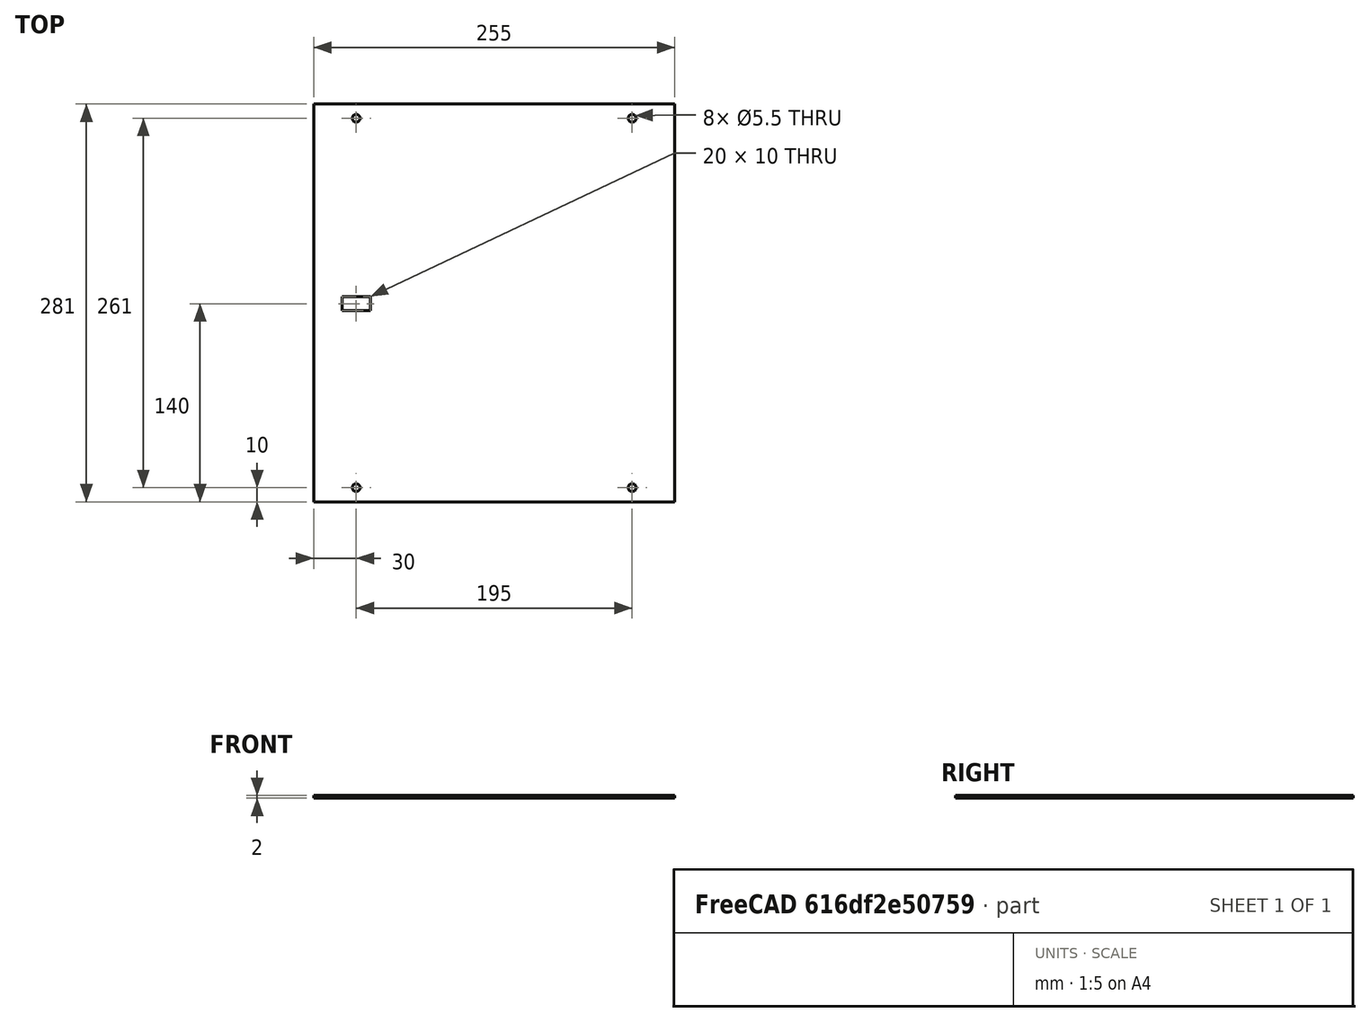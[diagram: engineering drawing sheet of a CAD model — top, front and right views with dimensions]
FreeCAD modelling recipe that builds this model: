
FCSTD DOCUMENT  (FreeCAD 0.15R4671 (Git))
Label: top
License: All rights reserved
LicenseURL: http://en.wikipedia.org/wiki/All_rights_reserved
objects: Drawing::FeatureViewPython×15, Part::Cut×6, Part::Cylinder×4, Part::Box×2, Drawing::FeatureViewPart×1, Drawing::FeaturePage×1
note: 12 computed .brp shape members not serialized (recipe doc carries the construction recipe); baked Part::Feature solids carry a one-line shape summary decoded from their .brp

FEATURE [Part::Box] Box  label="Cube"
  Height = 2
  Length = 255
  Placement = pos=(0,0,1.5332e-08) rot=(0,0,1;0rad)
  Width = 281
FEATURE [Part::Cylinder] Cylinder
  Angle = 360
  Height = 10
  Placement = pos=(30,10,-5) rot=(0,0,1;0rad)
  Radius = 2.75
FEATURE [Part::Cylinder] Cylinder001
  Angle = 360
  Height = 10
  Placement = pos=(30,271,-5) rot=(0,0,1;0rad)
  Radius = 2.75
FEATURE [Part::Cylinder] Cylinder002
  Angle = 360
  Height = 10
  Placement = pos=(225,10,-5) rot=(0,0,1;0rad)
  Radius = 2.75
FEATURE [Part::Cylinder] Cylinder003
  Angle = 360
  Height = 10
  Placement = pos=(225,271,-5) rot=(0,0,1;0rad)
  Radius = 2.75
FEATURE [Part::Cut] Cut
  Base = -> Box
  Tool = -> Cylinder
FEATURE [Part::Cut] Cut001
  Base = -> Cut
  Tool = -> Cylinder001
FEATURE [Part::Cut] Cut002
  Base = -> Cut001
  Tool = -> Cylinder002
FEATURE [Part::Cut] Cut003  label="top"
  Base = -> Cut002
  Tool = -> Cylinder003
FEATURE [Part::Box] Box001  label="Cube001"
  Height = 10
  Length = 20
  Placement = pos=(20,135,-5) rot=(0,0,1;0rad)
  Width = 10
FEATURE [Part::Cut] Cut004
  Base = -> Cut002
  Tool = -> Cylinder003
FEATURE [Part::Cut] Cut005
  Base = -> Cut003
  Tool = -> Box001
FEATURE [Drawing::FeatureViewPart] Ortho  label="Ortho_0_0"
  Direction = (0,0,1)
  HiddenWidth = 0.15
  LineWidth = 0.35
  Rotation = 0
  Scale = 0.5
  ShowHiddenLines = false
  ShowSmoothLines = false
  Source = -> Cut005
  Tolerance = 0.05
  ViewResult = <g id="Ortho_0_0"\n   transform="rotate(0,46.25,188.75) translate(46.25,188.75) scale(0.5,0.5)"\n  >\n<g   stroke="rgb(0, 0, 0)"\n   stroke-width="0.7"\n   stroke-linecap="butt"\n   stroke-linejoin="miter"\n   fill="none"\n   transform="scale(1,-1)"\n  >\n<path id= "1" d=" M 0 0 L 0 281 " />\n<path id= "2" d=" M 0 0 L 255 0 " />\n<path id= "3" d=" M 0 281 L 255 281 " />\n<path id= "4" d=" M 255 0 L 255 281 " />\n<circle cx ="30" cy ="10" r ="2.75" /><circle cx ="225" cy ="10" r ="2.75" /><path id= "7" d=" M 40 145 L 20 145 " />\n<path id= "8" d=" M 20 135 L 20 145 " />\n<path id= "9" d=" M 40 135 L 20 135 " />\n<path id= "10" d=" M 40 135 L 40 145 " />\n<circle cx ="225" cy ="271" r ="2.75" /><circle cx ="30" cy ="271" r ="2.75" /></g>\n</g>
  Visible = true
  X = 46.25
  Y = 188.75
FEATURE [Drawing::FeatureViewPython] dim001  # drawing view (typed FeaturePython)
  Rotation = 0
  ViewResult = <g> \n  <line x1="44.250000" y1="188.750000" x2="32.514934" y2="188.750000" style="stroke:rgb(0,0,255);stroke-width:0.50" />\n<line x1="44.250000" y1="48.250000" x2="32.514934" y2="48.250000" style="stroke:rgb(0,0,255);stroke-width:0.50" />\n<line x1="33.514934" y1="188.750000" x2="33.514934" y2="48.250000" style="stroke:rgb(0,0,255);stroke-width:0.50" /> \n  <polygon points="33.514934,48.250000 32.514934,51.250000 33.514934,52.250000 34.514934,51.250000" style="fill:rgb(0,0,255);stroke:rgb(0,0,255);stroke-width:0" /><polygon points="33.514934,188.750000 34.514934,185.750000 33.514934,184.750000 32.514934,185.750000" style="fill:rgb(0,0,255);stroke:rgb(0,0,255);stroke-width:0" /> \n  <text x="31.514934" y="118.500000" font-family="inherit" font-size="3.6" fill="rgb(0,0,255)" text-anchor="middle" transform="rotate(-90.000000 31.514934,118.500000)" >281</text> </g>
  Visible = true
  X = 0
  Y = 0
  arrowL1 = 3
  arrowL2 = 1
  arrowW = 2
  arrow_scheme = 0
  autoPlaceOffset = 2
  autoPlaceText = true
  click1_x = 33.5149
  click1_y = 120.857
  click2_x = 33.5149
  click2_y = 120.857
  comma_decimal_place = false
  dimension_line_overshoot = 1
  gap_datum_points = 2
  halfDimension_linear = false
  lineColor = rgb(0,0,255)
  strokeWidth = 0.5
  textFormat_linear = %(value)f
  textRenderer_color = rgb(0,0,255)
  textRenderer_family = inherit
  textRenderer_size = 3.6
  unit_custom_scale = 1
  unit_scheme = 0
FEATURE [Drawing::FeatureViewPython] dim002  # drawing view (typed FeaturePython)
  Rotation = 0
  ViewResult = <g> \n  <line x1="46.250000" y1="46.250000" x2="46.250000" y2="32.176400" style="stroke:rgb(0,0,255);stroke-width:0.50" />\n<line x1="173.750000" y1="46.250000" x2="173.750000" y2="32.176400" style="stroke:rgb(0,0,255);stroke-width:0.50" />\n<line x1="46.250000" y1="33.176400" x2="173.750000" y2="33.176400" style="stroke:rgb(0,0,255);stroke-width:0.50" /> \n  <polygon points="173.750000,33.176400 170.750000,32.176400 169.750000,33.176400 170.750000,34.176400" style="fill:rgb(0,0,255);stroke:rgb(0,0,255);stroke-width:0" /><polygon points="46.250000,33.176400 49.250000,34.176400 50.250000,33.176400 49.250000,32.176400" style="fill:rgb(0,0,255);stroke:rgb(0,0,255);stroke-width:0" /> \n  <text x="110.000000" y="31.176400" font-family="inherit" font-size="3.6" fill="rgb(0,0,255)" text-anchor="middle" transform="rotate(0.000000 110.000000,31.176400)" >255</text> </g>
  Visible = true
  X = 0
  Y = 0
  arrowL1 = 3
  arrowL2 = 1
  arrowW = 2
  arrow_scheme = 0
  autoPlaceOffset = 2
  autoPlaceText = true
  click1_x = 106.3
  click1_y = 33.1764
  click2_x = 106.3
  click2_y = 33.1764
  comma_decimal_place = false
  dimension_line_overshoot = 1
  gap_datum_points = 2
  halfDimension_linear = false
  lineColor = rgb(0,0,255)
  strokeWidth = 0.5
  textFormat_linear = %(value)f
  textRenderer_color = rgb(0,0,255)
  textRenderer_family = inherit
  textRenderer_size = 3.6
  unit_custom_scale = 1
  unit_scheme = 0
FEATURE [Drawing::FeatureViewPython] dim003  # drawing view (typed FeaturePython)
  Rotation = 0
  ViewResult = <g> \n  <line x1="66.250000" y1="114.250000" x2="66.250000" y2="105.638428" style="stroke:rgb(0,0,255);stroke-width:0.50" />\n<line x1="56.250000" y1="114.250000" x2="56.250000" y2="105.638428" style="stroke:rgb(0,0,255);stroke-width:0.50" />\n<line x1="66.250000" y1="106.638428" x2="56.250000" y2="106.638428" style="stroke:rgb(0,0,255);stroke-width:0.50" /> \n  <polygon points="56.250000,106.638428 53.250000,105.638428 52.250000,106.638428 53.250000,107.638428" style="fill:rgb(0,0,255);stroke:rgb(0,0,255);stroke-width:0" /><polygon points="66.250000,106.638428 69.250000,107.638428 70.250000,106.638428 69.250000,105.638428" style="fill:rgb(0,0,255);stroke:rgb(0,0,255);stroke-width:0" /> \n  <text x="61.250000" y="104.638428" font-family="inherit" font-size="3.6" fill="rgb(0,0,255)" text-anchor="middle" transform="rotate(0.000000 61.250000,104.638428)" >20</text> </g>
  Visible = true
  X = 0
  Y = 0
  arrowL1 = 3
  arrowL2 = 1
  arrowW = 2
  arrow_scheme = 0
  autoPlaceOffset = 2
  autoPlaceText = true
  click1_x = 62.6289
  click1_y = 106.638
  click2_x = 62.6289
  click2_y = 106.638
  comma_decimal_place = false
  dimension_line_overshoot = 1
  gap_datum_points = 2
  halfDimension_linear = false
  lineColor = rgb(0,0,255)
  strokeWidth = 0.5
  textFormat_linear = %(value)f
  textRenderer_color = rgb(0,0,255)
  textRenderer_family = inherit
  textRenderer_size = 3.6
  unit_custom_scale = 1
  unit_scheme = 0
FEATURE [Drawing::FeatureViewPython] dim004  # drawing view (typed FeaturePython)
  Rotation = 0
  ViewResult = <g> \n  <line x1="68.250000" y1="121.250000" x2="81.478770" y2="121.250000" style="stroke:rgb(0,0,255);stroke-width:0.50" />\n<line x1="68.250000" y1="116.250000" x2="81.478770" y2="116.250000" style="stroke:rgb(0,0,255);stroke-width:0.50" />\n<line x1="80.478770" y1="121.250000" x2="80.478770" y2="116.250000" style="stroke:rgb(0,0,255);stroke-width:0.50" /> \n  <polygon points="80.478770,116.250000 81.478770,113.250000 80.478770,112.250000 79.478770,113.250000" style="fill:rgb(0,0,255);stroke:rgb(0,0,255);stroke-width:0" /><polygon points="80.478770,121.250000 79.478770,124.250000 80.478770,125.250000 81.478770,124.250000" style="fill:rgb(0,0,255);stroke:rgb(0,0,255);stroke-width:0" /> \n  <text x="78.478770" y="118.750000" font-family="inherit" font-size="3.6" fill="rgb(0,0,255)" text-anchor="middle" transform="rotate(-90.000000 78.478770,118.750000)" >10</text> </g>
  Visible = true
  X = 0
  Y = 0
  arrowL1 = 3
  arrowL2 = 1
  arrowW = 2
  arrow_scheme = 0
  autoPlaceOffset = 2
  autoPlaceText = true
  click1_x = 80.4788
  click1_y = 118.572
  click2_x = 80.4788
  click2_y = 118.572
  comma_decimal_place = false
  dimension_line_overshoot = 1
  gap_datum_points = 2
  halfDimension_linear = false
  lineColor = rgb(0,0,255)
  strokeWidth = 0.5
  textFormat_linear = %(value)f
  textRenderer_color = rgb(0,0,255)
  textRenderer_family = inherit
  textRenderer_size = 3.6
  unit_custom_scale = 1
  unit_scheme = 0
FEATURE [Drawing::FeatureViewPython] dimStack001  # drawing view (typed FeaturePython)
  Rotation = 0
  ViewResult = <g> <line x1="160.750001" y1="183.750000" x2="186.299418" y2="183.750000" style="stroke:rgb(0,0,255);stroke-width:0.50" />\n<line x1="175.750001" y1="188.750000" x2="186.299418" y2="188.750000" style="stroke:rgb(0,0,255);stroke-width:0.50" />\n<line x1="185.299418" y1="183.750000" x2="185.299418" y2="188.750000" style="stroke:rgb(0,0,255);stroke-width:0.50" />\n<polygon points="185.299418,183.750000 186.299418,180.750000 185.299418,179.750000 184.299418,180.750000" style="fill:rgb(0,0,255);stroke:rgb(0,0,255);stroke-width:0" />\n<polygon points="185.299418,188.750000 184.299418,191.750000 185.299418,192.750000 186.299418,191.750000" style="fill:rgb(0,0,255);stroke:rgb(0,0,255);stroke-width:0" />\n<text x="183.299418" y="186.250000" font-family="inherit" font-size="3.6" fill="rgb(0,0,255)" text-anchor="middle" transform="rotate(-90.000000 183.299418,186.250000)" >10</text> </g> 
  Visible = true
  X = 0
  Y = 0
  arrowL1 = 3
  arrowL2 = 1
  arrowW = 2
  arrow_scheme = 0
  autoPlaceOffset = 2
  click1_x = 185.299
  click1_y = 187.612
  comma_decimal_place = false
  dimension_line_overshoot = 1
  gap_datum_points = 2
  lineColor = rgb(0,0,255)
  stack_offset = 7
  stack_offset0 = 0
  strokeWidth = 0.5
  textFormat_linear = %(value)f
  textRenderer_color = rgb(0,0,255)
  textRenderer_family = inherit
  textRenderer_size = 3.6
  unit_custom_scale = 1
  unit_scheme = 0
FEATURE [Drawing::FeatureViewPython] dimStack002  # drawing view (typed FeaturePython)
  Rotation = 0
  ViewResult = <g> <line x1="173.750000" y1="190.750001" x2="173.750000" y2="209.155734" style="stroke:rgb(0,0,255);stroke-width:0.50" />\n<line x1="158.750000" y1="187.125001" x2="158.750000" y2="209.155734" style="stroke:rgb(0,0,255);stroke-width:0.50" />\n<line x1="173.750000" y1="208.155734" x2="158.750000" y2="208.155734" style="stroke:rgb(0,0,255);stroke-width:0.50" />\n<polygon points="173.750000,208.155734 170.750000,207.155734 169.750000,208.155734 170.750000,209.155734" style="fill:rgb(0,0,255);stroke:rgb(0,0,255);stroke-width:0" />\n<polygon points="158.750000,208.155734 161.750000,209.155734 162.750000,208.155734 161.750000,207.155734" style="fill:rgb(0,0,255);stroke:rgb(0,0,255);stroke-width:0" />\n<text x="166.250000" y="206.155734" font-family="inherit" font-size="3.6" fill="rgb(0,0,255)" text-anchor="middle" transform="rotate(0.000000 166.250000,206.155734)" >30</text> </g> 
  Visible = true
  X = 0
  Y = 0
  arrowL1 = 3
  arrowL2 = 1
  arrowW = 2
  arrow_scheme = 0
  autoPlaceOffset = 2
  click1_x = 166.933
  click1_y = 208.156
  comma_decimal_place = false
  dimension_line_overshoot = 1
  gap_datum_points = 2
  lineColor = rgb(0,0,255)
  stack_offset = 7
  stack_offset0 = 0
  strokeWidth = 0.5
  textFormat_linear = %(value)f
  textRenderer_color = rgb(0,0,255)
  textRenderer_family = inherit
  textRenderer_size = 3.6
  unit_custom_scale = 1
  unit_scheme = 0
FEATURE [Drawing::FeatureViewPython] dimStack003  # drawing view (typed FeaturePython)
  Rotation = 0
  ViewResult = <g> <line x1="58.250001" y1="121.250000" x2="99.959080" y2="121.250000" style="stroke:rgb(0,0,255);stroke-width:0.50" />\n<line x1="48.250001" y1="188.750000" x2="99.959080" y2="188.750000" style="stroke:rgb(0,0,255);stroke-width:0.50" />\n<line x1="98.959080" y1="121.250000" x2="98.959080" y2="188.750000" style="stroke:rgb(0,0,255);stroke-width:0.50" />\n<polygon points="98.959080,121.250000 97.959080,124.250000 98.959080,125.250000 99.959080,124.250000" style="fill:rgb(0,0,255);stroke:rgb(0,0,255);stroke-width:0" />\n<polygon points="98.959080,188.750000 99.959080,185.750000 98.959080,184.750000 97.959080,185.750000" style="fill:rgb(0,0,255);stroke:rgb(0,0,255);stroke-width:0" />\n<text x="96.959080" y="155.000000" font-family="inherit" font-size="3.6" fill="rgb(0,0,255)" text-anchor="middle" transform="rotate(-90.000000 96.959080,155.000000)" >135</text> </g> 
  Visible = true
  X = 0
  Y = 0
  arrowL1 = 3
  arrowL2 = 1
  arrowW = 2
  arrow_scheme = 0
  autoPlaceOffset = 2
  click1_x = 98.9591
  click1_y = 136.367
  comma_decimal_place = false
  dimension_line_overshoot = 1
  gap_datum_points = 2
  lineColor = rgb(0,0,255)
  stack_offset = 7
  stack_offset0 = 0
  strokeWidth = 0.5
  textFormat_linear = %(value)f
  textRenderer_color = rgb(0,0,255)
  textRenderer_family = inherit
  textRenderer_size = 3.6
  unit_custom_scale = 1
  unit_scheme = 0
FEATURE [Drawing::FeatureViewPython] dimStack004  # drawing view (typed FeaturePython)
  Rotation = 0
  ViewResult = <g> <line x1="56.250000" y1="123.250000" x2="56.250000" y2="130.784437" style="stroke:rgb(0,0,255);stroke-width:0.50" />\n<line x1="56.250000" y1="129.784437" x2="46.250000" y2="129.784437" style="stroke:rgb(0,0,255);stroke-width:0.50" />\n<polygon points="56.250000,129.784437 59.250000,130.784437 60.250000,129.784437 59.250000,128.784437" style="fill:rgb(0,0,255);stroke:rgb(0,0,255);stroke-width:0" />\n<polygon points="46.250000,129.784437 43.250000,128.784437 42.250000,129.784437 43.250000,130.784437" style="fill:rgb(0,0,255);stroke:rgb(0,0,255);stroke-width:0" />\n<text x="51.250000" y="127.784437" font-family="inherit" font-size="3.6" fill="rgb(0,0,255)" text-anchor="middle" transform="rotate(0.000000 51.250000,127.784437)" >20</text> </g> 
  Visible = true
  X = 0
  Y = 0
  arrowL1 = 3
  arrowL2 = 1
  arrowW = 2
  arrow_scheme = 0
  autoPlaceOffset = 2
  click1_x = 52.2657
  click1_y = 129.784
  comma_decimal_place = false
  dimension_line_overshoot = 1
  gap_datum_points = 2
  lineColor = rgb(0,0,255)
  stack_offset = 7
  stack_offset0 = 0
  strokeWidth = 0.5
  textFormat_linear = %(value)f
  textRenderer_color = rgb(0,0,255)
  textRenderer_family = inherit
  textRenderer_size = 3.6
  unit_custom_scale = 1
  unit_scheme = 0
FEATURE [Drawing::FeatureViewPython] dimStack005  # drawing view (typed FeaturePython)
  Rotation = 0
  ViewResult = <g> <line x1="173.750000" y1="50.250001" x2="173.750000" y2="73.173715" style="stroke:rgb(0,0,255);stroke-width:0.50" />\n<line x1="158.750000" y1="56.625001" x2="158.750000" y2="73.173715" style="stroke:rgb(0,0,255);stroke-width:0.50" />\n<line x1="173.750000" y1="72.173715" x2="158.750000" y2="72.173715" style="stroke:rgb(0,0,255);stroke-width:0.50" />\n<polygon points="173.750000,72.173715 170.750000,71.173715 169.750000,72.173715 170.750000,73.173715" style="fill:rgb(0,0,255);stroke:rgb(0,0,255);stroke-width:0" />\n<polygon points="158.750000,72.173715 161.750000,73.173715 162.750000,72.173715 161.750000,71.173715" style="fill:rgb(0,0,255);stroke:rgb(0,0,255);stroke-width:0" />\n<text x="166.250000" y="70.173715" font-family="inherit" font-size="3.6" fill="rgb(0,0,255)" text-anchor="middle" transform="rotate(0.000000 166.250000,70.173715)" >30</text> </g> 
  Visible = true
  X = 0
  Y = 0
  arrowL1 = 3
  arrowL2 = 1
  arrowW = 2
  arrow_scheme = 0
  autoPlaceOffset = 2
  click1_x = 162.45
  click1_y = 72.1737
  comma_decimal_place = false
  dimension_line_overshoot = 1
  gap_datum_points = 2
  lineColor = rgb(0,0,255)
  stack_offset = 7
  stack_offset0 = 0
  strokeWidth = 0.5
  textFormat_linear = %(value)f
  textRenderer_color = rgb(0,0,255)
  textRenderer_family = inherit
  textRenderer_size = 3.6
  unit_custom_scale = 1
  unit_scheme = 0
FEATURE [Drawing::FeatureViewPython] dimStack006  # drawing view (typed FeaturePython)
  Rotation = 0
  ViewResult = <g> <line x1="61.250000" y1="56.625001" x2="61.250000" y2="65.650722" style="stroke:rgb(0,0,255);stroke-width:0.50" />\n<line x1="46.250000" y1="50.250001" x2="46.250000" y2="65.650722" style="stroke:rgb(0,0,255);stroke-width:0.50" />\n<line x1="61.250000" y1="64.650722" x2="46.250000" y2="64.650722" style="stroke:rgb(0,0,255);stroke-width:0.50" />\n<polygon points="61.250000,64.650722 58.250000,63.650722 57.250000,64.650722 58.250000,65.650722" style="fill:rgb(0,0,255);stroke:rgb(0,0,255);stroke-width:0" />\n<polygon points="46.250000,64.650722 49.250000,65.650722 50.250000,64.650722 49.250000,63.650722" style="fill:rgb(0,0,255);stroke:rgb(0,0,255);stroke-width:0" />\n<text x="53.750000" y="62.650722" font-family="inherit" font-size="3.6" fill="rgb(0,0,255)" text-anchor="middle" transform="rotate(0.000000 53.750000,62.650722)" >30</text> </g> 
  Visible = true
  X = 0
  Y = 0
  arrowL1 = 3
  arrowL2 = 1
  arrowW = 2
  arrow_scheme = 0
  autoPlaceOffset = 2
  click1_x = 53.6013
  click1_y = 64.6507
  comma_decimal_place = false
  dimension_line_overshoot = 1
  gap_datum_points = 2
  lineColor = rgb(0,0,255)
  stack_offset = 7
  stack_offset0 = 0
  strokeWidth = 0.5
  textFormat_linear = %(value)f
  textRenderer_color = rgb(0,0,255)
  textRenderer_family = inherit
  textRenderer_size = 3.6
  unit_custom_scale = 1
  unit_scheme = 0
FEATURE [Drawing::FeatureViewPython] dimStack007  # drawing view (typed FeaturePython)
  Rotation = 0
  ViewResult = <g> <line x1="61.250000" y1="183.124999" x2="61.250000" y2="168.972626" style="stroke:rgb(0,0,255);stroke-width:0.50" />\n<line x1="46.250000" y1="186.749999" x2="46.250000" y2="168.972626" style="stroke:rgb(0,0,255);stroke-width:0.50" />\n<line x1="61.250000" y1="169.972626" x2="46.250000" y2="169.972626" style="stroke:rgb(0,0,255);stroke-width:0.50" />\n<polygon points="61.250000,169.972626 58.250000,168.972626 57.250000,169.972626 58.250000,170.972626" style="fill:rgb(0,0,255);stroke:rgb(0,0,255);stroke-width:0" />\n<polygon points="46.250000,169.972626 49.250000,170.972626 50.250000,169.972626 49.250000,168.972626" style="fill:rgb(0,0,255);stroke:rgb(0,0,255);stroke-width:0" />\n<text x="53.750000" y="167.972626" font-family="inherit" font-size="3.6" fill="rgb(0,0,255)" text-anchor="middle" transform="rotate(0.000000 53.750000,167.972626)" >30</text> </g> 
  Visible = true
  X = 0
  Y = 0
  arrowL1 = 3
  arrowL2 = 1
  arrowW = 2
  arrow_scheme = 0
  autoPlaceOffset = 2
  click1_x = 52.1908
  click1_y = 169.973
  comma_decimal_place = false
  dimension_line_overshoot = 1
  gap_datum_points = 2
  lineColor = rgb(0,0,255)
  stack_offset = 7
  stack_offset0 = 0
  strokeWidth = 0.5
  textFormat_linear = %(value)f
  textRenderer_color = rgb(0,0,255)
  textRenderer_family = inherit
  textRenderer_size = 3.6
  unit_custom_scale = 1
  unit_scheme = 0
FEATURE [Drawing::FeatureViewPython] dimStack008  # drawing view (typed FeaturePython)
  Rotation = 0
  ViewResult = <g> <line x1="64.625001" y1="53.250000" x2="78.110680" y2="53.250000" style="stroke:rgb(0,0,255);stroke-width:0.50" />\n<line x1="48.250001" y1="48.250000" x2="78.110680" y2="48.250000" style="stroke:rgb(0,0,255);stroke-width:0.50" />\n<line x1="77.110680" y1="53.250000" x2="77.110680" y2="48.250000" style="stroke:rgb(0,0,255);stroke-width:0.50" />\n<polygon points="77.110680,53.250000 76.110680,56.250000 77.110680,57.250000 78.110680,56.250000" style="fill:rgb(0,0,255);stroke:rgb(0,0,255);stroke-width:0" />\n<polygon points="77.110680,48.250000 78.110680,45.250000 77.110680,44.250000 76.110680,45.250000" style="fill:rgb(0,0,255);stroke:rgb(0,0,255);stroke-width:0" />\n<text x="75.110680" y="50.750000" font-family="inherit" font-size="3.6" fill="rgb(0,0,255)" text-anchor="middle" transform="rotate(-90.000000 75.110680,50.750000)" >10</text> </g> 
  Visible = true
  X = 0
  Y = 0
  arrowL1 = 3
  arrowL2 = 1
  arrowW = 2
  arrow_scheme = 0
  autoPlaceOffset = 2
  click1_x = 77.1107
  click1_y = 52.661
  comma_decimal_place = false
  dimension_line_overshoot = 1
  gap_datum_points = 2
  lineColor = rgb(0,0,255)
  stack_offset = 7
  stack_offset0 = 0
  strokeWidth = 0.5
  textFormat_linear = %(value)f
  textRenderer_color = rgb(0,0,255)
  textRenderer_family = inherit
  textRenderer_size = 3.6
  unit_custom_scale = 1
  unit_scheme = 0
FEATURE [Drawing::FeatureViewPython] dimStack009  # drawing view (typed FeaturePython)
  Rotation = 0
  ViewResult = <g> <line x1="175.750001" y1="48.250000" x2="187.194080" y2="48.250000" style="stroke:rgb(0,0,255);stroke-width:0.50" />\n<line x1="162.125001" y1="53.250000" x2="187.194080" y2="53.250000" style="stroke:rgb(0,0,255);stroke-width:0.50" />\n<line x1="186.194080" y1="48.250000" x2="186.194080" y2="53.250000" style="stroke:rgb(0,0,255);stroke-width:0.50" />\n<polygon points="186.194080,48.250000 187.194080,45.250000 186.194080,44.250000 185.194080,45.250000" style="fill:rgb(0,0,255);stroke:rgb(0,0,255);stroke-width:0" />\n<polygon points="186.194080,53.250000 185.194080,56.250000 186.194080,57.250000 187.194080,56.250000" style="fill:rgb(0,0,255);stroke:rgb(0,0,255);stroke-width:0" />\n<text x="184.194080" y="50.750000" font-family="inherit" font-size="3.6" fill="rgb(0,0,255)" text-anchor="middle" transform="rotate(-90.000000 184.194080,50.750000)" >10</text> </g> 
  Visible = true
  X = 0
  Y = 0
  arrowL1 = 3
  arrowL2 = 1
  arrowW = 2
  arrow_scheme = 0
  autoPlaceOffset = 2
  click1_x = 186.194
  click1_y = 53.8364
  comma_decimal_place = false
  dimension_line_overshoot = 1
  gap_datum_points = 2
  lineColor = rgb(0,0,255)
  stack_offset = 7
  stack_offset0 = 0
  strokeWidth = 0.5
  textFormat_linear = %(value)f
  textRenderer_color = rgb(0,0,255)
  textRenderer_family = inherit
  textRenderer_size = 3.6
  unit_custom_scale = 1
  unit_scheme = 0
FEATURE [Drawing::FeatureViewPython] dimStack010  # drawing view (typed FeaturePython)
  Rotation = 0
  ViewResult = <g> <line x1="48.250001" y1="188.750000" x2="78.580867" y2="188.750000" style="stroke:rgb(0,0,255);stroke-width:0.50" />\n<line x1="64.625001" y1="183.750000" x2="78.580867" y2="183.750000" style="stroke:rgb(0,0,255);stroke-width:0.50" />\n<line x1="77.580867" y1="188.750000" x2="77.580867" y2="183.750000" style="stroke:rgb(0,0,255);stroke-width:0.50" />\n<polygon points="77.580867,188.750000 76.580867,191.750000 77.580867,192.750000 78.580867,191.750000" style="fill:rgb(0,0,255);stroke:rgb(0,0,255);stroke-width:0" />\n<polygon points="77.580867,183.750000 78.580867,180.750000 77.580867,179.750000 76.580867,180.750000" style="fill:rgb(0,0,255);stroke:rgb(0,0,255);stroke-width:0" />\n<text x="75.580867" y="186.250000" font-family="inherit" font-size="3.6" fill="rgb(0,0,255)" text-anchor="middle" transform="rotate(-90.000000 75.580867,186.250000)" >10</text> </g> 
  Visible = true
  X = 0
  Y = 0
  arrowL1 = 3
  arrowL2 = 1
  arrowW = 2
  arrow_scheme = 0
  autoPlaceOffset = 2
  click1_x = 77.5809
  click1_y = 185.019
  comma_decimal_place = false
  dimension_line_overshoot = 1
  gap_datum_points = 2
  lineColor = rgb(0,0,255)
  stack_offset = 7
  stack_offset0 = 0
  strokeWidth = 0.5
  textFormat_linear = %(value)f
  textRenderer_color = rgb(0,0,255)
  textRenderer_family = inherit
  textRenderer_size = 3.6
  unit_custom_scale = 1
  unit_scheme = 0
FEATURE [Drawing::FeatureViewPython] dia001  # drawing view (typed FeaturePython)
  Rotation = 0
  ViewResult = <g>  <circle cx ="61.250000" cy ="183.750000" r="0.250000" stroke="none" fill="rgb(0,0,255)" /> \n<line x1="74.994838" y1="169.737532" x2="60.287147" y2="184.731601" style="stroke:rgb(0,0,255);stroke-width:0.50" />\n<polygon points="62.212853,182.768399 65.027513,181.326982 65.013879,179.912834 63.599731,179.926469" style="fill:rgb(0,0,255);stroke:rgb(0,0,255);stroke-width:0" />\n<polygon points="60.287147,184.731601 57.472487,186.173018 57.486121,187.587166 58.900269,187.573531" style="fill:rgb(0,0,255);stroke:rgb(0,0,255);stroke-width:0" />\n<line x1="74.994838" y1="169.737532" x2="80.637083" y2="169.737532" style="stroke:rgb(0,0,255);stroke-width:0.50" />\n<text x="77.815960" y="167.737532" font-family="inherit" font-size="3.6" fill="rgb(0,0,255)" text-anchor="middle" transform="rotate(0.000000 77.815960,167.737532)" >Ø5.5</text> </g>
  Visible = true
  X = 0
  Y = 0
  arrowL1 = 3
  arrowL2 = 1
  arrowW = 2
  arrow_scheme = 0
  autoPlaceOffset = 2
  autoPlaceText = true
  centerPointDia = 0.5
  click1_x = 74.9948
  click1_y = 169.738
  click2_x = 80.6371
  click2_y = 170.443
  click3_x = 80.6371
  click3_y = 170.443
  comma_decimal_place = false
  lineColor = rgb(0,0,255)
  strokeWidth = 0.5
  textFormat_circular = Ø%(value)3.3f
  textRenderer_color = rgb(0,0,255)
  textRenderer_family = inherit
  textRenderer_size = 3.6
  unit_custom_scale = 1
  unit_scheme = 0
FEATURE [Drawing::FeaturePage] Page
  EditableTexts = Fichou Dimitri | OCLab top | Aluminium - 2 mm thick | Professur für Lebensmittelwissenschaften | Prof. Dr. Gertrud Morlock | A4 | X / Y | SCALE | PART NUMBER | DRAWING NUMBER | YYYY-MM-DD | A
  Group = -> [Ortho,dim001,dim002,dim003,dim004,dimStack001,dimStack002,dimStack003,dimStack004,dimStack005,dimStack006,dimStack007,dimStack008,dimStack009,dimStack010,dia001]
  Template = <path>
note: 1 file-system path scrubbed to <path> (originals preserved in the JSON sidecar)
